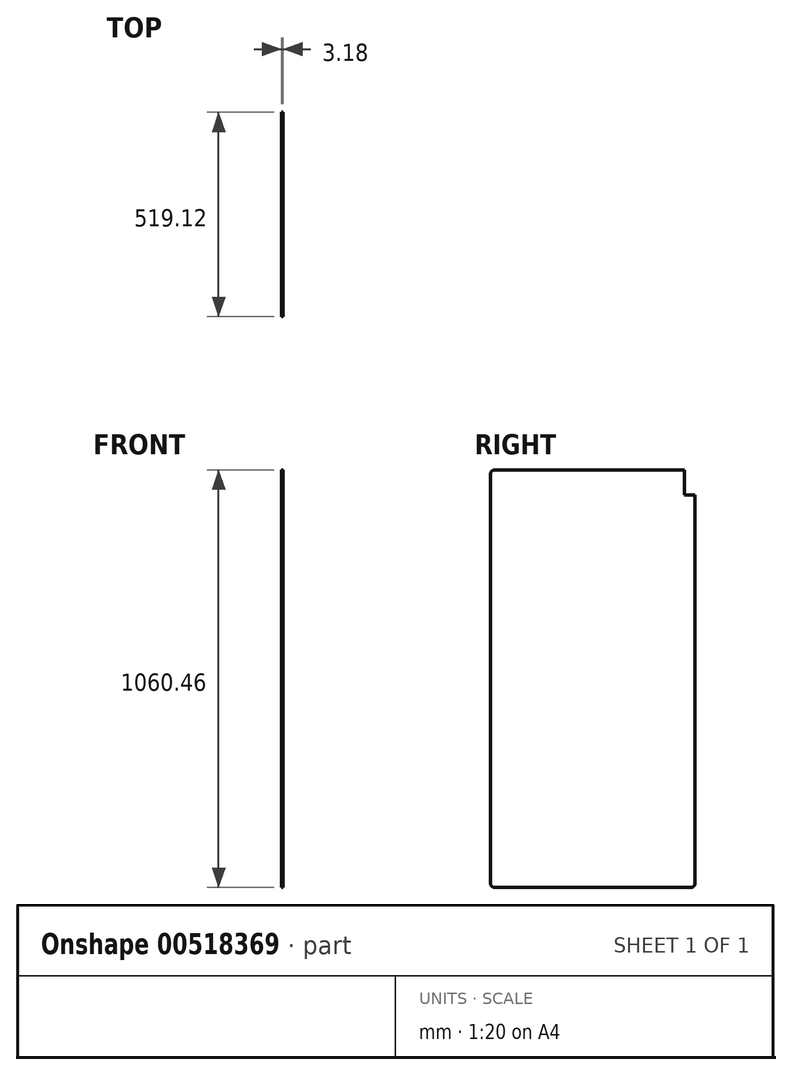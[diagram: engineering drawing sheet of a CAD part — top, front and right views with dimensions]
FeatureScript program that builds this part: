
annotation { "Feature Type Name" : "Feature", "Feature Type Description" : "" }
export const myFeature = defineFeature(function(context is Context, id is Id, definition is map)
    precondition{}
    {
        {
            var Q0;
            Q0=qCreatedBy(makeId("Right.planeOp"),FACE);
            var sketch = newSketch(context, id + "F0", { "sketchPlane" : qUnion([Q0])});
            skLineSegment(sketch, "E0.bottom", {"start": v(-259.56, 530.23) * mm, "end": v(259.56, 530.22) * mm});
            skLineSegment(sketch, "E0.top", {"start": v(-259.56, -530.23) * mm, "end": v(259.56, -530.23) * mm});
            skLineSegment(sketch, "E0.left", {"start": v(-259.56, 530.23) * mm, "end": v(-259.56, -530.23) * mm});
            skLineSegment(sketch, "E0.right", {"start": v(259.56, 530.23) * mm, "end": v(259.56, -530.23) * mm});
            skSolve(sketch);
        }
        {
            var Q0;
            Q0=makeQuery(id+"F0.imprint","IMPRINT",FACE,{"disambiguationData":[TD([[makeQuery(id+"F0.imprint","IMPRINT",EDGE,{"derivedFrom":sQuery(id+"F0.wireOp",EDGE,"E0.bottom")}),-1.0]])]});
            extrude(context, id + "F1", {"entities" : qUnion([Q0]), "endBound" : BoundingType.SYMMETRIC, "depth" : 3.17 * mm, "offsetDistance" : 25.4 * mm});
        }
        {
            var Q0;
            Q0=makeQuery(id+"F1.opExtrude","CAP_FACE",FACE,{"disambiguationData":[OSD([sQuery(id+"F0.wireOp",EDGE,"E0.bottom"),sQuery(id+"F0.wireOp",EDGE,"E0.top"),sQuery(id+"F0.wireOp",EDGE,"E0.left"),sQuery(id+"F0.wireOp",EDGE,"E0.right")])],"isStart":false});
            var sketch = newSketch(context, id + "F2", { "sketchPlane" : qUnion([Q0])});
            skLineSegment(sketch, "E1.bottom", {"start": v(259.56, 530.22) * mm, "end": v(232.57, 530.22) * mm});
            skLineSegment(sketch, "E1.top", {"start": v(259.56, 466.72) * mm, "end": v(232.57, 466.72) * mm});
            skLineSegment(sketch, "E1.left", {"start": v(259.56, 530.22) * mm, "end": v(259.56, 466.72) * mm});
            skLineSegment(sketch, "E1.right", {"start": v(232.57, 530.22) * mm, "end": v(232.57, 466.72) * mm});
            skSolve(sketch);
        }
        {
            var Q0;
            Q0 = qSketchRegion(id + "F2", true);
            extrude(context, id + "F3", {"entities" : qUnion([Q0]), "operationType" : NewBodyOperationType.REMOVE, "endBound" : BoundingType.THROUGH_ALL, "oppositeDirection" : true, "depth" : 25.4 * mm, "offsetDistance" : 25.4 * mm});
        }
        {
            var Q0;
            Q0=makeQuery(id+"F1.opExtrude","SWEPT_EDGE",EDGE,{"disambiguationData":[OSD([sQuery(id+"F0.wireOp",EDGE,"E0.bottom"),sQuery(id+"F0.wireOp",EDGE,"E0.left")])]});
            var Q1;
            Q1=makeQuery(id+"F1.opExtrude","SWEPT_EDGE",EDGE,{"disambiguationData":[OSD([sQuery(id+"F0.wireOp",EDGE,"E0.top"),sQuery(id+"F0.wireOp",EDGE,"E0.left")])]});
            var Q2;
            Q2=makeQuery(id+"F1.opExtrude","SWEPT_EDGE",EDGE,{"disambiguationData":[OSD([sQuery(id+"F0.wireOp",EDGE,"E0.top"),sQuery(id+"F0.wireOp",EDGE,"E0.right")])]});
            var Q3;
            Q3=makeQuery(id+"F3.boolean.opBoolean","COPY",EDGE,{"derivedFrom":makeQuery(id+"F3.opExtrude","SWEPT_EDGE",EDGE,{"disambiguationData":[OSD([sQuery(id+"F0.wireOp",EDGE,"E0.bottom"),sQuery(id+"F2.wireOp",EDGE,"E1.bottom"),sQuery(id+"F2.wireOp",EDGE,"E1.right")])]})});
            var Q4;
            Q4=makeQuery(id+"F3.boolean.opBoolean","COPY",EDGE,{"derivedFrom":makeQuery(id+"F3.opExtrude","SWEPT_EDGE",EDGE,{"disambiguationData":[OSD([sQuery(id+"F0.wireOp",EDGE,"E0.right"),sQuery(id+"F2.wireOp",EDGE,"E1.top"),sQuery(id+"F2.wireOp",EDGE,"E1.left")])]})});
            fillet(context, id + "F4", {"entities" : qUnion([Q0, Q1, Q2, Q3, Q4]), "radius" : 9.52 * mm, "tangentPropagation" : true, "allowEdgeOverflow" : false});
        }
    });
